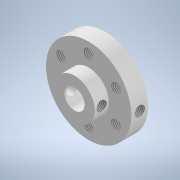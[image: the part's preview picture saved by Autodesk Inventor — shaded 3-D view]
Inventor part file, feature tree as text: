
AUTODESK INVENTOR PART (.ipt)
format: ipt  version: 2020.3 (Build 243373000, 373)  size: 204,800 bytes
history: native  units: mm
features: thread x10, extrude x6, sketch x6, pattern_circular x1, plane x1
ambient origin geometry x8: Origin, YZ Plane, XZ Plane, XY Plane, X Axis, Y Axis, Z Axis, Center Point
bodies: Solid1 (feature_tree)
feature tree (24):
  extrude  "Extrusion1"  Depth=5.0mm TaperAngle=0.0deg
  extrude  "Extrusion2"  Depth=6.0mm
  extrude  "Extrusion3"  Depth=19.0mm
  pattern_circular  "Circular Pattern1"  Count=6 Angle=360.0deg
  extrude  "Extrusion4"  Depth=10.0mm
  plane  "Work Plane1"
  extrude  "Extrusion5"  Depth=10.0mm TaperAngle=0.0deg
  extrude  "Extrusion6"  Depth=10.0mm
  thread  "Thread1"  [1 undecoded]
  thread  "Thread2"  [1 undecoded]
  thread  "Thread3"  [1 undecoded]
  thread  "Thread4"  [1 undecoded]
  thread  "Thread5"  [1 undecoded]
  thread  "Thread6"  [1 undecoded]
  thread  "Thread7"  [1 undecoded]
  thread  "Thread9"  [1 undecoded]
  thread  "Thread11"  [1 undecoded]
  thread  "Thread12"  [1 undecoded]
  sketch  "Sketch1"  dims[d0=25.4mm d1=5.0mm d2=0.0mm]
  sketch  "Sketch2"  dims[d3=12.0mm d4=6.0mm]
  sketch  "Sketch3"  dims[d5=4.2mm d6=0.0mm d7=19.0mm]
  sketch  "Sketch4"  dims[d8=3.0mm]
  sketch  "Sketch6"  dims[d9=5.0mm d10=0.0mm d11=60.0mm d12=360.0deg]
  sketch  "Sketch7"  dims[d14=19.0mm d15=3.0mm d16=10.0mm d17=0.0mm d18=12.7mm d19=2.5mm d20=3.0mm d21=25.4mm d22=0.0mm d23=3.0mm d24=2.1mm d25=25.4mm d26=0.0mm d27=10.222mm d28=0.0mm d29=5.0mm d30=0.0mm d31=5.0mm d32=0.0mm d33=5.0mm d34=0.0mm d35=5.0mm d36=0.0mm d37=5.0mm d38=0.0mm d39=3.402mm d40=0.0mm d43=5.0mm d44=0.0mm d47=10.222mm d48=0.0mm d49=3.402mm d50=0.0mm]
note: 10 required parameter values undecoded (feature->parameter linkage not recoverable at this tier; creation-order binding heuristic only, values carry confidence <= 0.55)
